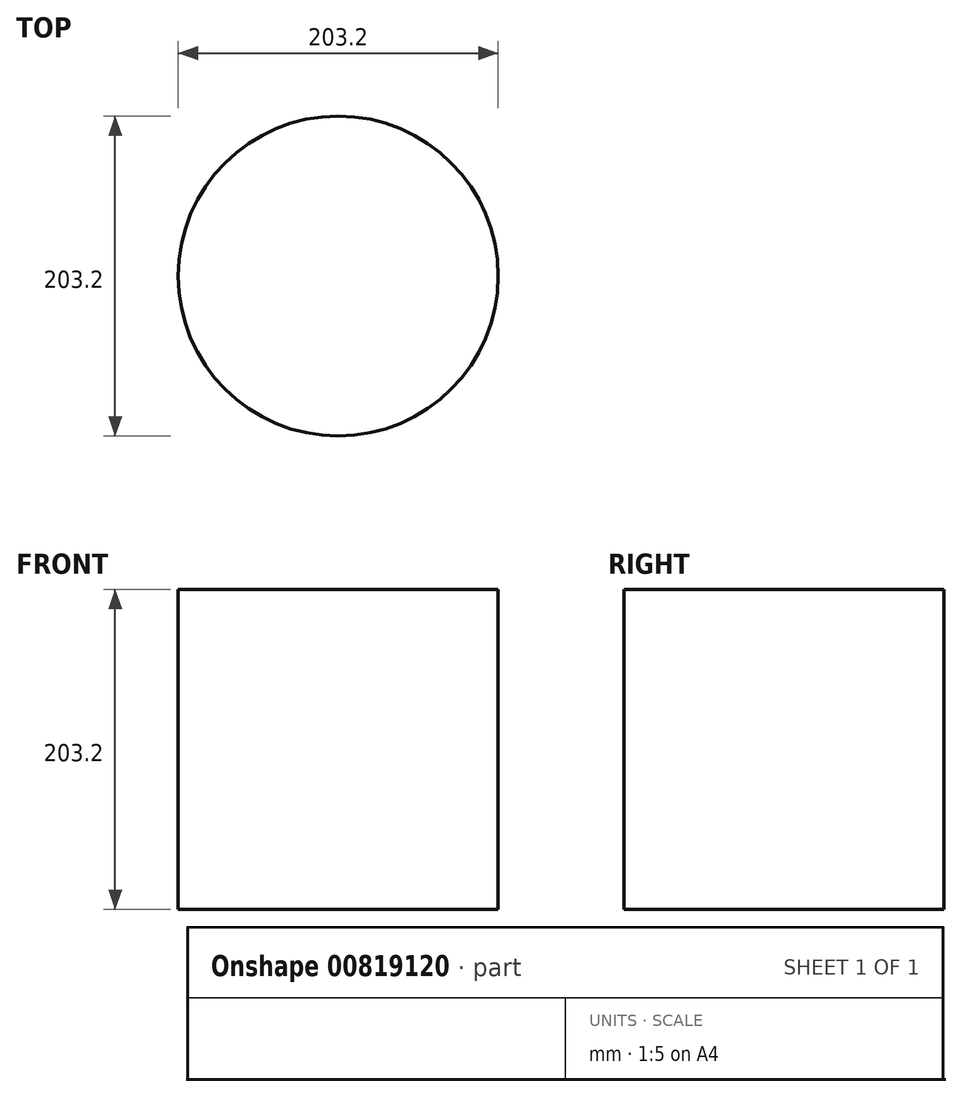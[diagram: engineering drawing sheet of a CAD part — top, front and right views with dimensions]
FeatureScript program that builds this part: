
annotation { "Feature Type Name" : "Feature", "Feature Type Description" : "" }
export const myFeature = defineFeature(function(context is Context, id is Id, definition is map)
    precondition{}
    {
        {
            var Q0;
            Q0=qCreatedBy(makeId("Top.planeOp"),FACE);
            var sketch = newSketch(context, id + "F0", { "sketchPlane" : qUnion([Q0])});
            skCircle(sketch, "E0", {"center": v(0, 0) * mm, "radius": 101.6 * mm});
            skSolve(sketch);
        }
        {
            var Q0;
            Q0 = qSketchRegion(id + "F0", true);
            extrude(context, id + "F1", {"entities" : qUnion([Q0]), "depth" : 203.2 * mm, "offsetDistance" : 25.4 * mm});
        }
        {
            var Q0;
            Q0=qCreatedBy(makeId("Top.planeOp"),FACE);
            var sketch = newSketch(context, id + "F2", { "sketchPlane" : qUnion([Q0])});
            skLineSegment(sketch, "E1", {"start": v(0, 87.55) * mm, "end": v(0, -154.74) * mm, "construction": true});
            skSolve(sketch);
        }
        {
            var Q0;
            Q0=sQuery(id+"F2.wireOp",EDGE,"E1");
            var Q1;
            Q1=qCreatedBy(makeId("Right.planeOp"),FACE);
            cPlane(context, id + "F3", {"entities" : qUnion([Q0, Q1]), "cplaneType" : CPlaneType.LINE_ANGLE, "offset" : 25.4 * mm, "angle" : 15 * degree, "width" : 152.4 * mm, "height" : 152.4 * mm});
        }
    });
